# Revit family: 306_P6_W_E-BAC
name_source: partatom
category: Pipe Accessories
units: mm (PartAtom-declared; Revit-internal decimal feet)

## family parameters
Always vertical = Yes
Cut with Voids When Loaded = No
Part Type = Valve - Breaks Into
Round Connector Dimension = Use Diameter
Shared = No
Work Plane-Based = No

## types (5) — shared parameters
CAT0 = Yes
Description = Pressure-independent Belimo Energy Valve™, Flange, DN 65-150
FT = 30 mm  [stored 0.0984252 ft]
FT1 = 2 mm  [stored 0.00656168 ft]
FT1__ve = -2 mm  [stored -0.00656168 ft]
FTT = 28 mm  [stored 0.0918635 ft]
FTT__ve = -28 mm  [stored -0.0918635 ft]
L1 = 10 mm  [stored 0.0328084 ft]
L11 = 30 mm  [stored 0.0984252 ft]
L11__ve = -30 mm  [stored -0.0984252 ft]
L2D_Min = 3048 mm
Manufacturer = Belimo
QmdConnectorList = 301;D;302;D
R22 = 15 mm  [stored 0.0492126 ft]
R5 = 5 mm  [stored 0.0164042 ft]
X1 = 40 mm  [stored 0.131234 ft]
magiPartTypeId = 306
magiProductFamilyId = P6*W*E-BAC
zero-valued in all types: MC_Default_elevation

## per-type parameters (varying)
- P6065W800EV-BAC: D=65 mm; DX=65 mm; FD=185 mm; FD1=52 mm  [stored 0.170604 ft]; FDD=144 mm; H1=35 mm; H2=20 mm  [stored 0.0656168 ft]; H3=30 mm  [stored 0.0984252 ft]; HH=27 mm; HHH=35 mm; HZ1=44 mm; HZ3=43 mm; HZ4=26 mm  [stored 0.0853018 ft]; K=145 mm; L2D=454 mm; L4=43 mm; L44=65 mm; L45=48 mm; L5=130 mm; L54=143 mm; L55=133 mm; L6=36 mm; L7=72 mm; LL=227 mm; LX=78 mm; LX4=26 mm  [stored 0.0853018 ft]; R1=85 mm; R11=91 mm; R3=52 mm  [stored 0.170604 ft]; R4=46 mm; R44=23 mm; W2D=65 mm
- P6150W4500EV-BAC: D=150 mm; DX=150 mm; FD=282 mm; FD1=120 mm; FDD=280 mm; H1=77 mm; H2=23 mm; H3=33 mm; HH=25 mm  [stored 0.082021 ft]; HHH=32 mm; HZ1=100 mm; HZ3=38 mm; HZ4=24 mm; K=240 mm; L2D=767 mm; L4=85 mm; L44=127 mm; L45=93 mm; L5=255 mm; L54=280 mm; L55=221 mm; L6=71 mm; L7=142 mm; LL=384 mm; LX=153 mm; LX4=51 mm; R1=195 mm; R11=210 mm; R3=120 mm; R4=105 mm; R44=53 mm; W2D=150 mm
- P6125W3100EV-BAC: D=125 mm; DX=125 mm; FD=252 mm; FD1=100 mm; FDD=240 mm; H1=65 mm; H2=22 mm; H3=32 mm; HH=29 mm; HHH=37 mm; HZ1=83 mm; HZ3=43 mm; HZ4=26 mm  [stored 0.0853018 ft]; K=210 mm; L2D=640 mm; L4=68 mm; L44=102 mm; L45=75 mm; L5=204 mm; L54=224 mm; L55=181 mm; L6=57 mm; L7=113 mm; LL=320 mm; LX=122 mm; LX4=41 mm; R1=163 mm; R11=175 mm; R3=100 mm; R4=88 mm; R44=44 mm; W2D=125 mm
- P6100W2000EV-BAC: D=100 mm; DX=100 mm; FD=229 mm; FD1=80 mm; FDD=200 mm; H1=52 mm  [stored 0.170604 ft]; H2=22 mm; H3=32 mm; HH=26 mm  [stored 0.0853018 ft]; HHH=34 mm; HZ1=67 mm; HZ3=42 mm  [stored 0.137795 ft]; HZ4=26 mm  [stored 0.0853018 ft]; K=180 mm; L2D=582 mm; L4=60 mm; L44=90 mm; L45=66 mm; L5=181 mm; L54=199 mm; L55=169 mm; L6=50 mm  [stored 0.164042 ft]; L7=100 mm; LL=291 mm; LX=108 mm; LX4=36 mm; R1=130 mm; R11=140 mm; R3=80 mm; R4=70 mm; R44=35 mm; W2D=100 mm
- P6080W1100EV-BAC: D=80 mm; DX=80 mm; FD=200 mm; FD1=64 mm; FDD=168 mm; H1=42 mm  [stored 0.137795 ft]; H2=20 mm  [stored 0.0656168 ft]; H3=30 mm  [stored 0.0984252 ft]; HH=25 mm  [stored 0.082021 ft]; HHH=33 mm; HZ1=54 mm; HZ3=39 mm; HZ4=25 mm  [stored 0.082021 ft]; K=160 mm; L2D=499 mm; L4=49 mm; L44=74 mm; L45=54 mm; L5=148 mm; L54=162 mm; L55=145 mm; L6=41 mm; L7=82 mm; LL=250 mm; LX=89 mm; LX4=30 mm  [stored 0.0984252 ft]; R1=104 mm; R11=112 mm; R3=64 mm; R4=56 mm; R44=28 mm  [stored 0.0918635 ft]; W2D=80 mm

note: column(s) folded — value = type name in every type: magiProductCode, magiProductId

note: [stored X ft] marks values corroborated as IEEE doubles in the binary element streams (Revit-internal decimal feet)

## geometry (parser evidence)
native form markers: Sweep x3
no freeform markers — native parametric forms only
